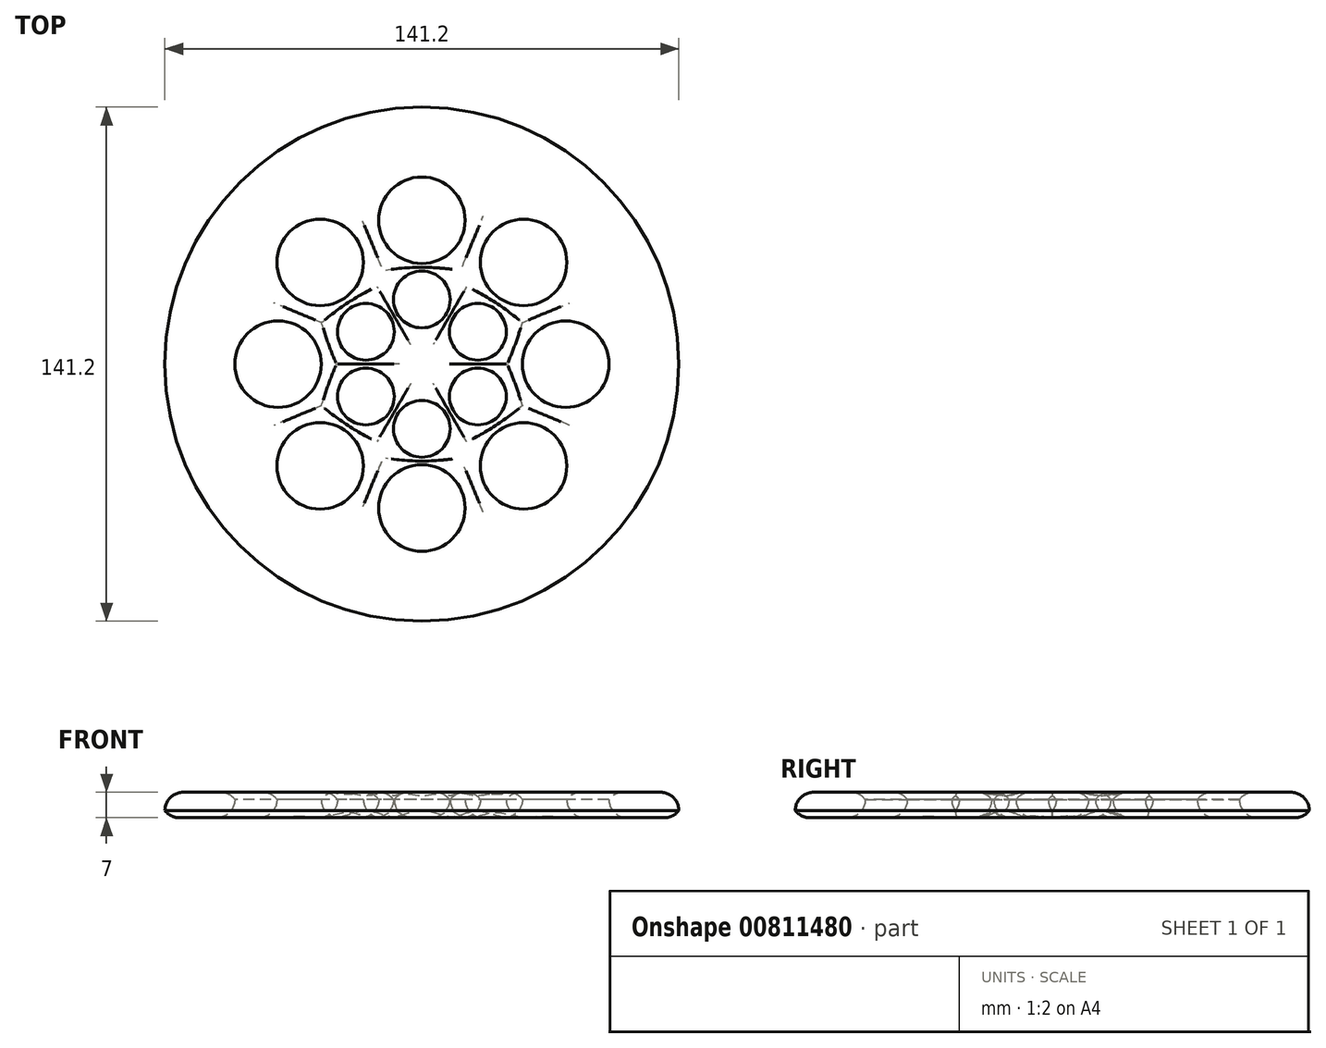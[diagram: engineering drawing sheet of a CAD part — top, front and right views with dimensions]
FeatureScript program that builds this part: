
annotation { "Feature Type Name" : "Feature", "Feature Type Description" : "" }
export const myFeature = defineFeature(function(context is Context, id is Id, definition is map)
    precondition{}
    {
        {
            var Q0;
            Q0=qCreatedBy(makeId("Top.planeOp"),FACE);
            var sketch = newSketch(context, id + "F0", { "sketchPlane" : qUnion([Q0])});
            skCircle(sketch, "E0", {"center": v(0, 0) * mm, "radius": 70.6 * mm});
            skCircle(sketch, "E1", {"center": v(0, 0) * mm, "radius": 51.78 * mm});
            skCircle(sketch, "E2", {"center": v(0, 39.52) * mm, "radius": 11.88 * mm});
            skCircle(sketch, "E3.1.0", {"center": v(-27.95, 27.95) * mm, "radius": 11.88 * mm});
            skCircle(sketch, "E3.2.0", {"center": v(-39.52, 0) * mm, "radius": 11.88 * mm});
            skCircle(sketch, "E3.3.0", {"center": v(-27.95, -27.95) * mm, "radius": 11.88 * mm});
            skCircle(sketch, "E3.4.0", {"center": v(0, -39.52) * mm, "radius": 11.88 * mm});
            skCircle(sketch, "E3.5.0", {"center": v(27.95, -27.95) * mm, "radius": 11.88 * mm});
            skCircle(sketch, "E3.6.0", {"center": v(39.52, 0) * mm, "radius": 11.88 * mm});
            skCircle(sketch, "E3.7.0", {"center": v(27.95, 27.95) * mm, "radius": 11.88 * mm});
            skCircle(sketch, "E4.cCircle", {"center": v(0, 0) * mm, "radius": 27.75 * mm, "construction": true});
            skLineSegment(sketch, "E4.0", {"start": v(13.42, 24.3) * mm, "end": v(26.66, 7.7) * mm});
            skLineSegment(sketch, "E4.1", {"start": v(26.66, 7.7) * mm, "end": v(24.3, -13.42) * mm});
            skLineSegment(sketch, "E4.2", {"start": v(24.3, -13.42) * mm, "end": v(7.7, -26.66) * mm});
            skLineSegment(sketch, "E4.3", {"start": v(7.7, -26.66) * mm, "end": v(-13.42, -24.3) * mm});
            skLineSegment(sketch, "E4.4", {"start": v(-13.42, -24.3) * mm, "end": v(-26.66, -7.7) * mm});
            skLineSegment(sketch, "E4.5", {"start": v(-26.66, -7.7) * mm, "end": v(-24.3, 13.42) * mm});
            skLineSegment(sketch, "E4.6", {"start": v(-24.3, 13.42) * mm, "end": v(-7.7, 26.66) * mm});
            skLineSegment(sketch, "E4.7", {"start": v(-7.7, 26.66) * mm, "end": v(13.42, 24.3) * mm});
            skCircle(sketch, "E5", {"center": v(0, 17.77) * mm, "radius": 7.8 * mm});
            skCircle(sketch, "E6.1.0", {"center": v(-15.39, 8.88) * mm, "radius": 7.8 * mm});
            skCircle(sketch, "E6.2.0", {"center": v(-15.39, -8.88) * mm, "radius": 7.8 * mm});
            skCircle(sketch, "E6.3.0", {"center": v(0, -17.77) * mm, "radius": 7.8 * mm});
            skCircle(sketch, "E6.4.0", {"center": v(15.39, -8.88) * mm, "radius": 7.8 * mm});
            skCircle(sketch, "E6.5.0", {"center": v(15.39, 8.88) * mm, "radius": 7.8 * mm});
            skSolve(sketch);
        }
        {
            var Q0;
            Q0=makeQuery(id+"F0.imprint","IMPRINT",FACE,{"disambiguationData":[TD([[makeQuery(id+"F0.imprint","IMPRINT",EDGE,{"derivedFrom":sQuery(id+"F0.wireOp",EDGE,"E1")}),1.0]])]});
            var Q1;
            Q1=makeQuery(id+"F0.imprint","IMPRINT",FACE,{"disambiguationData":[TD([[makeQuery(id+"F0.imprint","IMPRINT",EDGE,{"derivedFrom":sQuery(id+"F0.wireOp",EDGE,"E0")}),1.0]])]});
            var Q2;
            Q2=makeQuery(id+"F0.imprint","IMPRINT",FACE,{"disambiguationData":[TD([[makeQuery(id+"F0.imprint","IMPRINT",EDGE,{"derivedFrom":sQuery(id+"F0.wireOp",EDGE,"E4.0")}),-1.0]])]});
            extrude(context, id + "F1", {"entities" : qUnion([Q0, Q1, Q2]), "depth" : 7 * mm, "offsetDistance" : 25 * mm});
        }
        {
            var Q0;
            Q0=makeQuery(id+"F1.opExtrude","CAP_EDGE",EDGE,{"disambiguationData":[OSD([sQuery(id+"F0.wireOp",EDGE,"E0")])],"isStart":false});
            fillet(context, id + "F2", {"entities" : qUnion([Q0]), "radius" : 5 * mm, "tangentPropagation" : true, "allowEdgeOverflow" : false});
        }
        {
            var Q0;
            Q0=makeQuery(id+"F1.opExtrude","CAP_EDGE",EDGE,{"disambiguationData":[OSD([sQuery(id+"F0.wireOp",EDGE,"E0")])],"isStart":true});
            fillet(context, id + "F3", {"entities" : qUnion([Q0]), "radius" : 5 * mm, "tangentPropagation" : true, "allowEdgeOverflow" : false});
        }
        {
            var Q0;
            Q0=makeQuery(id+"F1.opExtrude","CAP_EDGE",EDGE,{"disambiguationData":[OSD([sQuery(id+"F0.wireOp",EDGE,"E3.4.0")])],"isStart":true});
            var Q1;
            Q1=makeQuery(id+"F1.opExtrude","CAP_EDGE",EDGE,{"disambiguationData":[OSD([sQuery(id+"F0.wireOp",EDGE,"E6.3.0")])],"isStart":true});
            var Q2;
            Q2=makeQuery(id+"F1.opExtrude","CAP_EDGE",EDGE,{"disambiguationData":[OSD([sQuery(id+"F0.wireOp",EDGE,"E3.5.0")])],"isStart":true});
            var Q3;
            Q3=makeQuery(id+"F1.opExtrude","CAP_EDGE",EDGE,{"disambiguationData":[OSD([sQuery(id+"F0.wireOp",EDGE,"E3.3.0")])],"isStart":true});
            var Q4;
            Q4=makeQuery(id+"F1.opExtrude","CAP_EDGE",EDGE,{"disambiguationData":[OSD([sQuery(id+"F0.wireOp",EDGE,"E3.2.0")])],"isStart":true});
            var Q5;
            Q5=makeQuery(id+"F1.opExtrude","CAP_EDGE",EDGE,{"disambiguationData":[OSD([sQuery(id+"F0.wireOp",EDGE,"E3.1.0")])],"isStart":true});
            var Q6;
            Q6=makeQuery(id+"F1.opExtrude","CAP_EDGE",EDGE,{"disambiguationData":[OSD([sQuery(id+"F0.wireOp",EDGE,"E2")])],"isStart":true});
            var Q7;
            Q7=makeQuery(id+"F1.opExtrude","CAP_EDGE",EDGE,{"disambiguationData":[OSD([sQuery(id+"F0.wireOp",EDGE,"E3.7.0")])],"isStart":true});
            var Q8;
            Q8=makeQuery(id+"F1.opExtrude","CAP_EDGE",EDGE,{"disambiguationData":[OSD([sQuery(id+"F0.wireOp",EDGE,"E3.6.0")])],"isStart":true});
            var Q9;
            Q9=makeQuery(id+"F1.opExtrude","CAP_EDGE",EDGE,{"disambiguationData":[OSD([sQuery(id+"F0.wireOp",EDGE,"E6.5.0")])],"isStart":true});
            var Q10;
            Q10=makeQuery(id+"F1.opExtrude","CAP_EDGE",EDGE,{"disambiguationData":[OSD([sQuery(id+"F0.wireOp",EDGE,"E6.4.0")])],"isStart":true});
            var Q11;
            Q11=makeQuery(id+"F1.opExtrude","CAP_EDGE",EDGE,{"disambiguationData":[OSD([sQuery(id+"F0.wireOp",EDGE,"E6.2.0")])],"isStart":true});
            var Q12;
            Q12=makeQuery(id+"F1.opExtrude","CAP_EDGE",EDGE,{"disambiguationData":[OSD([sQuery(id+"F0.wireOp",EDGE,"E6.1.0")])],"isStart":true});
            var Q13;
            Q13=makeQuery(id+"F1.opExtrude","CAP_EDGE",EDGE,{"disambiguationData":[OSD([sQuery(id+"F0.wireOp",EDGE,"E5")])],"isStart":true});
            fillet(context, id + "F4", {"entities" : qUnion([Q0, Q1, Q2, Q3, Q4, Q5, Q6, Q7, Q8, Q9, Q10, Q11, Q12, Q13]), "radius" : 5 * mm, "tangentPropagation" : true, "allowEdgeOverflow" : false});
        }
        {
            var Q0;
            Q0=makeQuery(id+"F1.opExtrude","CAP_EDGE",EDGE,{"disambiguationData":[OSD([sQuery(id+"F0.wireOp",EDGE,"E3.4.0")])],"isStart":false});
            var Q1;
            Q1=makeQuery(id+"F1.opExtrude","CAP_EDGE",EDGE,{"disambiguationData":[OSD([sQuery(id+"F0.wireOp",EDGE,"E3.3.0")])],"isStart":false});
            var Q2;
            Q2=makeQuery(id+"F1.opExtrude","CAP_EDGE",EDGE,{"disambiguationData":[OSD([sQuery(id+"F0.wireOp",EDGE,"E3.2.0")])],"isStart":false});
            var Q3;
            Q3=makeQuery(id+"F1.opExtrude","CAP_EDGE",EDGE,{"disambiguationData":[OSD([sQuery(id+"F0.wireOp",EDGE,"E6.2.0")])],"isStart":false});
            var Q4;
            Q4=makeQuery(id+"F1.opExtrude","CAP_EDGE",EDGE,{"disambiguationData":[OSD([sQuery(id+"F0.wireOp",EDGE,"E6.3.0")])],"isStart":false});
            var Q5;
            Q5=makeQuery(id+"F1.opExtrude","CAP_EDGE",EDGE,{"disambiguationData":[OSD([sQuery(id+"F0.wireOp",EDGE,"E3.5.0")])],"isStart":false});
            var Q6;
            Q6=makeQuery(id+"F1.opExtrude","CAP_EDGE",EDGE,{"disambiguationData":[OSD([sQuery(id+"F0.wireOp",EDGE,"E6.4.0")])],"isStart":false});
            var Q7;
            Q7=makeQuery(id+"F1.opExtrude","CAP_EDGE",EDGE,{"disambiguationData":[OSD([sQuery(id+"F0.wireOp",EDGE,"E3.6.0")])],"isStart":false});
            var Q8;
            Q8=makeQuery(id+"F1.opExtrude","CAP_EDGE",EDGE,{"disambiguationData":[OSD([sQuery(id+"F0.wireOp",EDGE,"E3.7.0")])],"isStart":false});
            var Q9;
            Q9=makeQuery(id+"F1.opExtrude","CAP_EDGE",EDGE,{"disambiguationData":[OSD([sQuery(id+"F0.wireOp",EDGE,"E6.5.0")])],"isStart":false});
            var Q10;
            Q10=makeQuery(id+"F1.opExtrude","CAP_EDGE",EDGE,{"disambiguationData":[OSD([sQuery(id+"F0.wireOp",EDGE,"E5")])],"isStart":false});
            var Q11;
            Q11=makeQuery(id+"F1.opExtrude","CAP_EDGE",EDGE,{"disambiguationData":[OSD([sQuery(id+"F0.wireOp",EDGE,"E6.1.0")])],"isStart":false});
            var Q12;
            Q12=makeQuery(id+"F1.opExtrude","CAP_EDGE",EDGE,{"disambiguationData":[OSD([sQuery(id+"F0.wireOp",EDGE,"E3.1.0")])],"isStart":false});
            var Q13;
            Q13=makeQuery(id+"F1.opExtrude","CAP_EDGE",EDGE,{"disambiguationData":[OSD([sQuery(id+"F0.wireOp",EDGE,"E2")])],"isStart":false});
            fillet(context, id + "F5", {"entities" : qUnion([Q0, Q1, Q2, Q3, Q4, Q5, Q6, Q7, Q8, Q9, Q10, Q11, Q12, Q13]), "radius" : 5 * mm, "tangentPropagation" : true, "allowEdgeOverflow" : false});
        }
    });
